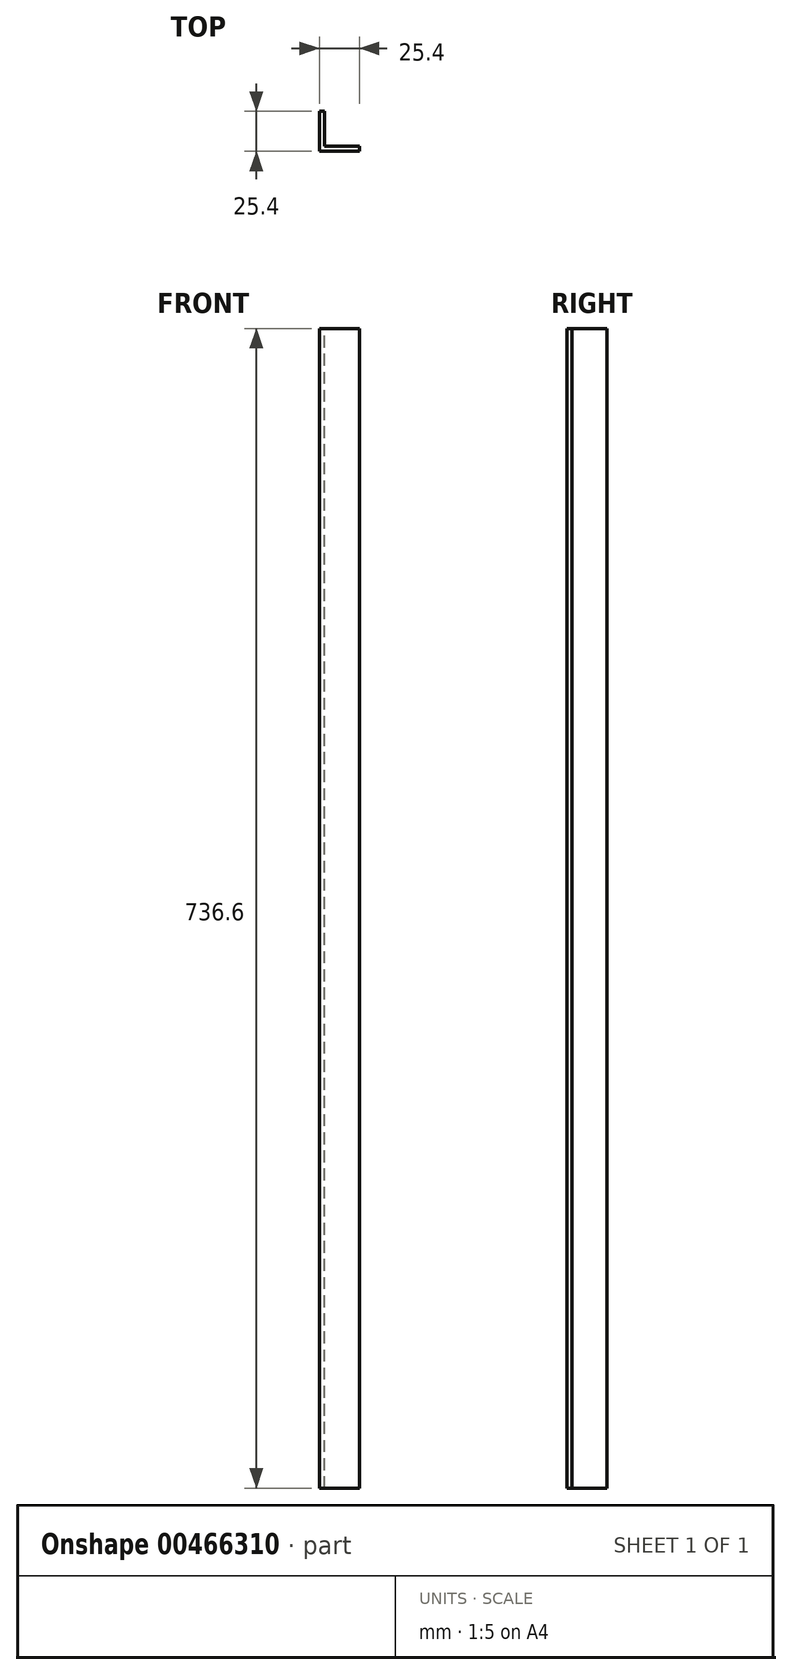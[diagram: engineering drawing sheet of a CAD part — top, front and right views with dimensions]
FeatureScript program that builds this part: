
annotation { "Feature Type Name" : "Feature", "Feature Type Description" : "" }
export const myFeature = defineFeature(function(context is Context, id is Id, definition is map)
    precondition{}
    {
        {
            var Q0;
            Q0=qCreatedBy(makeId("Top.planeOp"),FACE);
            var sketch = newSketch(context, id + "F0", { "sketchPlane" : qUnion([Q0])});
            skLineSegment(sketch, "E0", {"start": v(-290.33, 30.62) * mm, "end": v(-264.93, 30.62) * mm});
            skLineSegment(sketch, "E1", {"start": v(-290.33, 30.62) * mm, "end": v(-290.33, 56.02) * mm});
            skLineSegment(sketch, "E2", {"start": v(-264.93, 30.62) * mm, "end": v(-264.93, 33.8) * mm});
            skLineSegment(sketch, "E3", {"start": v(-290.33, 56.02) * mm, "end": v(-287.15, 56.02) * mm});
            skLineSegment(sketch, "E4", {"start": v(-287.15, 56.02) * mm, "end": v(-287.15, 33.8) * mm});
            skLineSegment(sketch, "E5", {"start": v(-287.15, 33.8) * mm, "end": v(-264.93, 33.8) * mm});
            skSolve(sketch);
        }
        {
            var Q0;
            Q0=makeQuery(id+"F0.imprint","IMPRINT",FACE,{"disambiguationData":[TD([[makeQuery(id+"F0.imprint","IMPRINT",EDGE,{"derivedFrom":sQuery(id+"F0.wireOp",EDGE,"E0")}),1.0]])]});
            extrude(context, id + "F1", {"entities" : qUnion([Q0]), "oppositeDirection" : true, "depth" : 730.25 * mm});
        }
        {
            var Q0;
            Q0=makeQuery(id+"F1.opExtrude","CAP_FACE",FACE,{"disambiguationData":[OSD([sQuery(id+"F0.wireOp",EDGE,"E0"),sQuery(id+"F0.wireOp",EDGE,"E1"),sQuery(id+"F0.wireOp",EDGE,"E2"),sQuery(id+"F0.wireOp",EDGE,"E3"),sQuery(id+"F0.wireOp",EDGE,"E4"),sQuery(id+"F0.wireOp",EDGE,"E5")])],"isStart":true});
            extrude(context, id + "F2", {"entities" : qUnion([Q0]), "operationType" : NewBodyOperationType.ADD, "depth" : 6.35 * mm});
        }
    });
